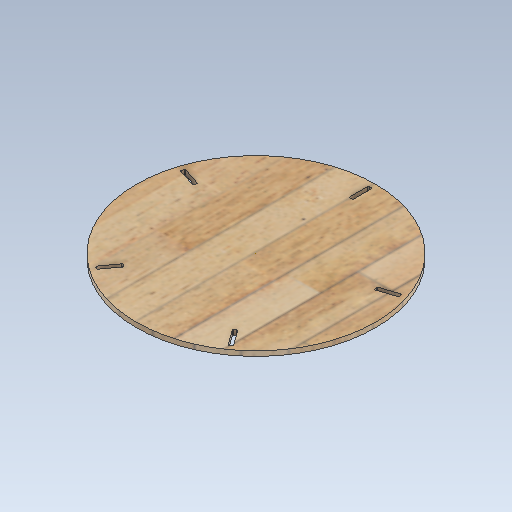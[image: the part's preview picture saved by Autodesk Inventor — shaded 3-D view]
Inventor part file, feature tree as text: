
AUTODESK INVENTOR PART (.ipt)
format: ipt  version: 2020 (Build 240168000, 168)  size: 270,848 bytes
history: native  units: mm
features: extrude x2, sketch x1
ambient origin geometry x8: Origin, YZ Plane, XZ Plane, XY Plane, X Axis, Y Axis, Z Axis, Center Point
bodies: Solid1 (feature_tree)
feature tree (3):
  extrude  "Extrusion1"  Depth=8.0mm TaperAngle=0.0deg
  extrude  "Extrusion2"  Depth=1.333333mm
  sketch  "Sketch1"  dims[d0=400.0mm d1=8.0mm d2=0.0mm d3=191.4mm d4=6.5mm d6=1.333333mm d7=30.0mm d12=0.0mm d13=0.0mm]
